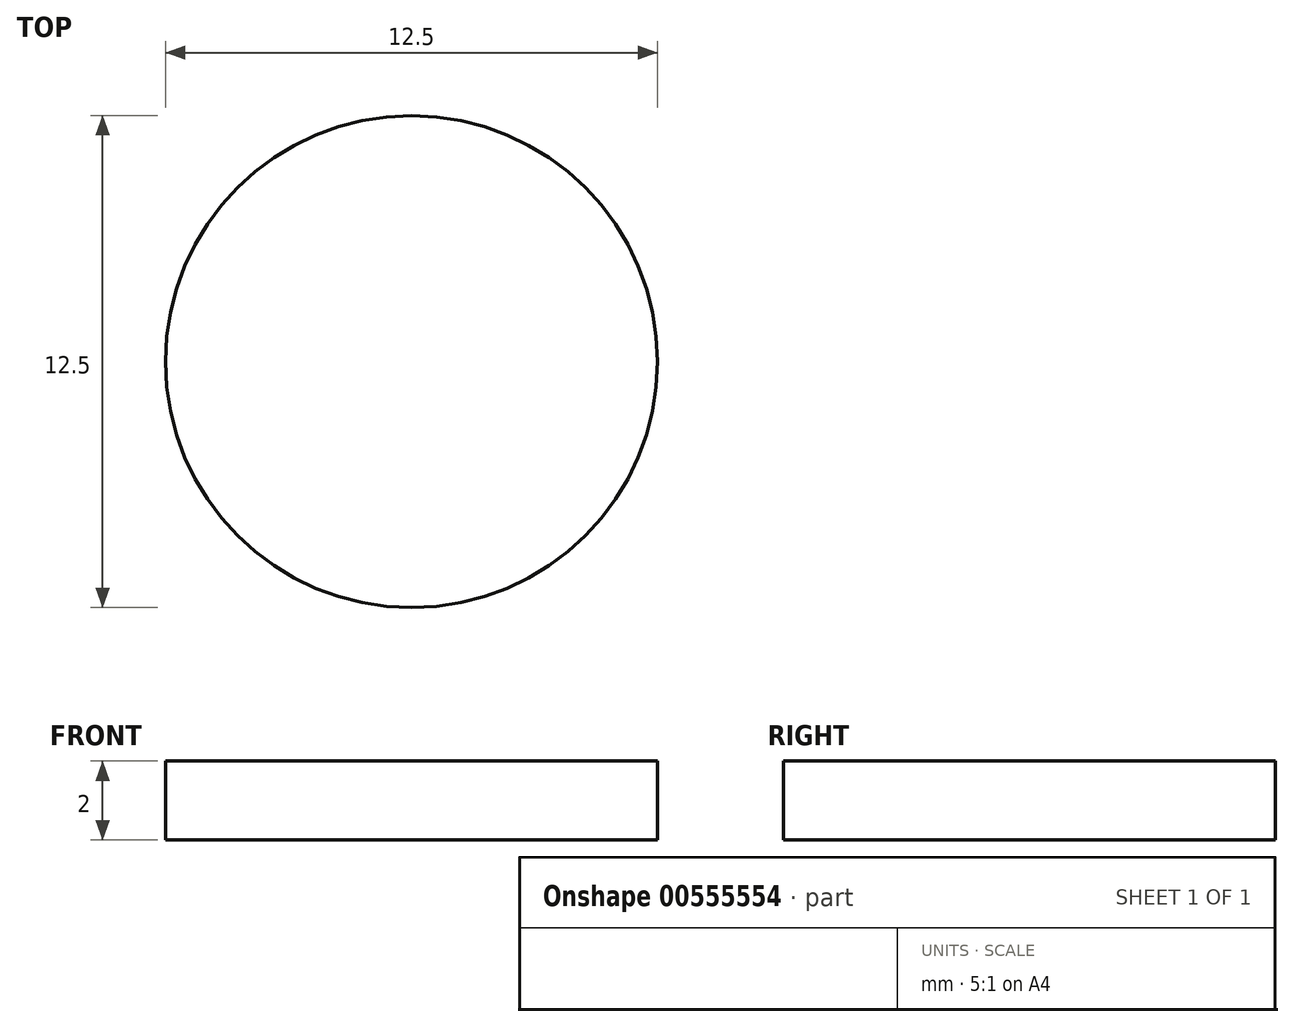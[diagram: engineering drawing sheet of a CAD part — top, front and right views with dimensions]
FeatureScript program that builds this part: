
annotation { "Feature Type Name" : "Feature", "Feature Type Description" : "" }
export const myFeature = defineFeature(function(context is Context, id is Id, definition is map)
    precondition{}
    {
        {
            var Q0;
            Q0=qCreatedBy(makeId("Top.planeOp"),FACE);
            var sketch = newSketch(context, id + "F0", { "sketchPlane" : qUnion([Q0])});
            skCircle(sketch, "E0", {"center": v(0, 0) * mm, "radius": 6.25 * mm});
            skSolve(sketch);
        }
        {
            var Q0;
            Q0 = qSketchRegion(id + "F0", true);
            extrude(context, id + "F1", {"entities" : qUnion([Q0]), "depth" : 2 * mm, "offsetDistance" : 25.4 * mm});
        }
    });
